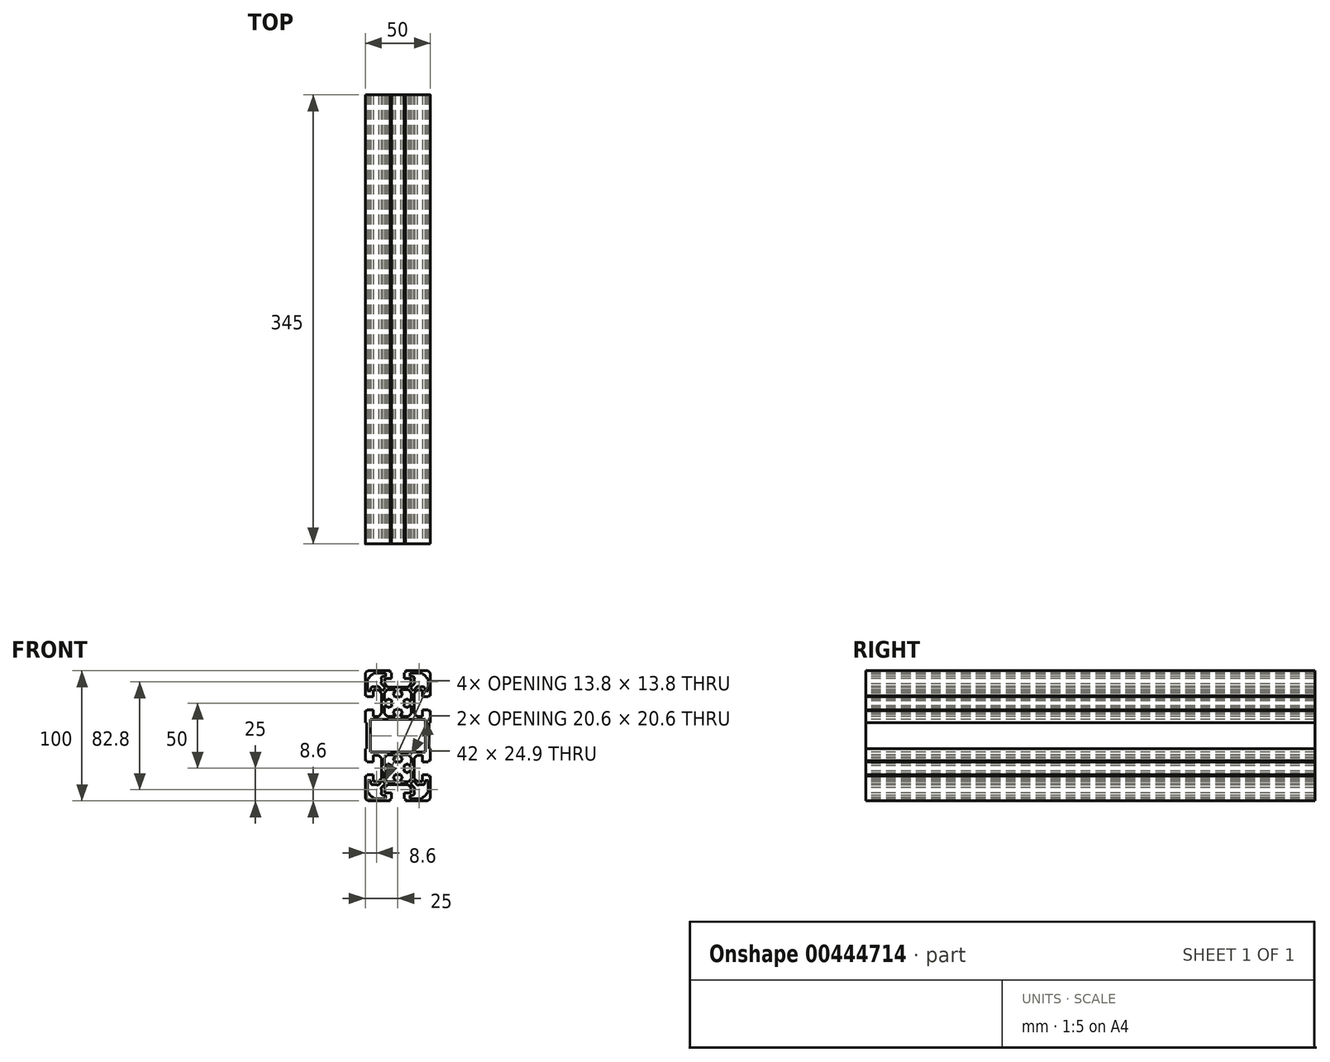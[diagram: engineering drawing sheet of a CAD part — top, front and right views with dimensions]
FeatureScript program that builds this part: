
annotation { "Feature Type Name" : "Feature", "Feature Type Description" : "" }
export const myFeature = defineFeature(function(context is Context, id is Id, definition is map)
    precondition{}
    {
        {
            var Q0;
            Q0=qCreatedBy(makeId("Front.planeOp"),FACE);
            var sketch = newSketch(context, id + "F0", { "sketchPlane" : qUnion([Q0])});
            skLineSegment(sketch, "E0", {"start": v(0, 0) * mm, "end": v(0, 25) * mm, "construction": true});
            skLineSegment(sketch, "E1", {"start": v(0, 0) * mm, "end": v(0, -25) * mm, "construction": true});
            skCircle(sketch, "E2", {"center": v(0, 25) * mm, "radius": 10 * mm});
            skCircle(sketch, "E3", {"center": v(0, -25) * mm, "radius": 10 * mm});
            skLineSegment(sketch, "E4.bottom", {"start": v(25, 50) * mm, "end": v(-25, 50) * mm});
            skLineSegment(sketch, "E4.top", {"start": v(25, -50) * mm, "end": v(-25, -50) * mm});
            skLineSegment(sketch, "E4.left", {"start": v(25, 50) * mm, "end": v(25, -50) * mm});
            skLineSegment(sketch, "E4.right", {"start": v(-25, 50) * mm, "end": v(-25, -50) * mm});
            skPoint(sketch, "E4.middle", {"position": v(0, 0) * mm});
            skSolve(sketch);
        }
        {
            var Q0;
            Q0=makeQuery(id+"F0.imprint","IMPRINT",FACE,{"disambiguationData":[TD([[makeQuery(id+"F0.imprint","IMPRINT",EDGE,{"derivedFrom":sQuery(id+"F0.wireOp",EDGE,"E2")}),-1.0]])]});
            cPlane(context, id + "F1", {"entities" : qUnion([Q0]), "cplaneType" : CPlaneType.OFFSET, "offset" : 25 * mm, "width" : 150 * mm, "height" : 150 * mm});
        }
        {
            var Q0;
            Q0=qCreatedBy(makeId("Front.planeOp"),FACE);
            var sketch = newSketch(context, id + "F2", { "sketchPlane" : qUnion([Q0])});
            skArc(sketch, "E5", {"start": v(-18.8, 37.67) * mm, "mid": v(-20.11, 37.42) * mm, "end": v(-20.7, 36.23) * mm});
            skArc(sketch, "E6", {"start": v(20.7, 36.23) * mm, "mid": v(20.11, 37.42) * mm, "end": v(18.8, 37.67) * mm});
            skArc(sketch, "E7", {"start": v(12.9, -40.52) * mm, "mid": v(12.51, -42.15) * mm, "end": v(12.67, -43.8) * mm});
            skArc(sketch, "E8", {"start": v(22, -50) * mm, "mid": v(24.12, -49.12) * mm, "end": v(25, -47) * mm});
            skArc(sketch, "E9", {"start": v(19, -47.27) * mm, "mid": v(21.04, -46.04) * mm, "end": v(22.27, -44) * mm});
            skArc(sketch, "E10", {"start": v(11.23, -45.7) * mm, "mid": v(12.42, -45.11) * mm, "end": v(12.67, -43.8) * mm});
            skArc(sketch, "E11", {"start": v(18.8, -37.67) * mm, "mid": v(20.11, -37.42) * mm, "end": v(20.7, -36.23) * mm});
            skArc(sketch, "E12", {"start": v(18.8, -37.67) * mm, "mid": v(17.14, -37.51) * mm, "end": v(15.52, -37.9) * mm});
            skArc(sketch, "E13", {"start": v(15.2, -37.85) * mm, "mid": v(15.35, -37.93) * mm, "end": v(15.52, -37.9) * mm});
            skArc(sketch, "E14", {"start": v(12.9, -40.52) * mm, "mid": v(12.93, -40.35) * mm, "end": v(12.84, -40.2) * mm});
            skArc(sketch, "E15", {"start": v(-4.53, -22.89) * mm, "mid": v(-5, -25) * mm, "end": v(-4.53, -27.11) * mm});
            skArc(sketch, "E16", {"start": v(4.53, -27.11) * mm, "mid": v(5, -25) * mm, "end": v(4.53, -22.89) * mm});
            skArc(sketch, "E17", {"start": v(-2.11, -29.53) * mm, "mid": v(0, -30) * mm, "end": v(2.11, -29.53) * mm});
            skArc(sketch, "E18", {"start": v(2.11, -20.47) * mm, "mid": v(0, -20) * mm, "end": v(-2.11, -20.47) * mm});
            skArc(sketch, "E19", {"start": v(-4.53, 27.11) * mm, "mid": v(-5, 25) * mm, "end": v(-4.53, 22.89) * mm});
            skArc(sketch, "E20", {"start": v(4.53, 22.89) * mm, "mid": v(5, 25) * mm, "end": v(4.53, 27.11) * mm});
            skArc(sketch, "E21", {"start": v(-2.11, 20.47) * mm, "mid": v(0, 20) * mm, "end": v(2.11, 20.47) * mm});
            skArc(sketch, "E22", {"start": v(15.52, 37.9) * mm, "mid": v(15.35, 37.93) * mm, "end": v(15.2, 37.84) * mm});
            skArc(sketch, "E23", {"start": v(15.52, 37.9) * mm, "mid": v(17.14, 37.51) * mm, "end": v(18.8, 37.67) * mm});
            skArc(sketch, "E24", {"start": v(2.11, 29.53) * mm, "mid": v(0, 30) * mm, "end": v(-2.11, 29.53) * mm});
            skArc(sketch, "E25", {"start": v(-12.67, -43.8) * mm, "mid": v(-12.51, -42.15) * mm, "end": v(-12.9, -40.52) * mm});
            skArc(sketch, "E26", {"start": v(-25, -47) * mm, "mid": v(-24.12, -49.12) * mm, "end": v(-22, -50) * mm});
            skArc(sketch, "E27", {"start": v(-12.67, -43.8) * mm, "mid": v(-12.42, -45.11) * mm, "end": v(-11.23, -45.7) * mm});
            skArc(sketch, "E28", {"start": v(-22.27, -44) * mm, "mid": v(-21.04, -46.04) * mm, "end": v(-19, -47.27) * mm});
            skArc(sketch, "E29", {"start": v(-20.7, -36.23) * mm, "mid": v(-20.11, -37.42) * mm, "end": v(-18.8, -37.67) * mm});
            skArc(sketch, "E30", {"start": v(-15.52, -37.9) * mm, "mid": v(-17.14, -37.51) * mm, "end": v(-18.8, -37.67) * mm});
            skArc(sketch, "E31", {"start": v(-12.84, -40.2) * mm, "mid": v(-12.93, -40.35) * mm, "end": v(-12.9, -40.52) * mm});
            skArc(sketch, "E32", {"start": v(-15.52, -37.9) * mm, "mid": v(-15.35, -37.93) * mm, "end": v(-15.2, -37.85) * mm});
            skArc(sketch, "E33", {"start": v(-18.8, 37.67) * mm, "mid": v(-17.14, 37.51) * mm, "end": v(-15.52, 37.9) * mm});
            skArc(sketch, "E34", {"start": v(-15.2, 37.84) * mm, "mid": v(-15.35, 37.93) * mm, "end": v(-15.52, 37.9) * mm});
            skArc(sketch, "E35", {"start": v(25, 47) * mm, "mid": v(24.12, 49.12) * mm, "end": v(22, 50) * mm});
            skArc(sketch, "E36", {"start": v(22.27, 44) * mm, "mid": v(21.04, 46.04) * mm, "end": v(19, 47.27) * mm});
            skArc(sketch, "E37", {"start": v(12.67, 43.8) * mm, "mid": v(12.42, 45.11) * mm, "end": v(11.23, 45.7) * mm});
            skArc(sketch, "E38", {"start": v(12.67, 43.8) * mm, "mid": v(12.51, 42.14) * mm, "end": v(12.9, 40.52) * mm});
            skArc(sketch, "E39", {"start": v(12.84, 40.2) * mm, "mid": v(12.93, 40.35) * mm, "end": v(12.9, 40.52) * mm});
            skArc(sketch, "E40", {"start": v(-22, 50) * mm, "mid": v(-24.12, 49.12) * mm, "end": v(-25, 47) * mm});
            skArc(sketch, "E41", {"start": v(-11.23, 45.7) * mm, "mid": v(-12.42, 45.11) * mm, "end": v(-12.67, 43.8) * mm});
            skArc(sketch, "E42", {"start": v(-12.9, 40.52) * mm, "mid": v(-12.93, 40.35) * mm, "end": v(-12.84, 40.2) * mm});
            skArc(sketch, "E43", {"start": v(-12.9, 40.52) * mm, "mid": v(-12.51, 42.14) * mm, "end": v(-12.67, 43.8) * mm});
            skArc(sketch, "E44", {"start": v(-19, 47.27) * mm, "mid": v(-21.04, 46.04) * mm, "end": v(-22.27, 44) * mm});
            skLineSegment(sketch, "E45", {"start": v(-9.54, 36.88) * mm, "end": v(-12.84, 40.2) * mm});
            skLineSegment(sketch, "E46", {"start": v(-25, 47) * mm, "end": v(-25, 30.8) * mm});
            skLineSegment(sketch, "E47", {"start": v(-23.3, 44) * mm, "end": v(-23.3, 34.5) * mm});
            skLineSegment(sketch, "E48", {"start": v(10.05, 39.8) * mm, "end": v(7.75, 37.5) * mm});
            skLineSegment(sketch, "E49", {"start": v(12.84, 40.2) * mm, "end": v(9.54, 36.88) * mm});
            skLineSegment(sketch, "E50", {"start": v(25, 30.8) * mm, "end": v(25, 47) * mm});
            skLineSegment(sketch, "E51", {"start": v(23.3, 34.5) * mm, "end": v(23.3, 44) * mm});
            skLineSegment(sketch, "E52", {"start": v(-7.75, 37.5) * mm, "end": v(-10.05, 39.8) * mm});
            skLineSegment(sketch, "E53", {"start": v(-2, 35.3) * mm, "end": v(-8.01, 35.3) * mm});
            skLineSegment(sketch, "E54", {"start": v(7.75, 37.5) * mm, "end": v(-7.75, 37.5) * mm});
            skLineSegment(sketch, "E55", {"start": v(-4.53, 22.89) * mm, "end": v(-7.7, 21.4) * mm});
            skLineSegment(sketch, "E56", {"start": v(-8.01, 14.7) * mm, "end": v(-2, 14.7) * mm});
            skLineSegment(sketch, "E57", {"start": v(-7.7, 28.6) * mm, "end": v(-4.53, 27.11) * mm});
            skLineSegment(sketch, "E58", {"start": v(-8.01, -35.3) * mm, "end": v(-2, -35.3) * mm});
            skLineSegment(sketch, "E59", {"start": v(-2, -14.7) * mm, "end": v(-8.01, -14.7) * mm});
            skLineSegment(sketch, "E60", {"start": v(-7.7, -21.4) * mm, "end": v(-4.53, -22.89) * mm});
            skLineSegment(sketch, "E61", {"start": v(-4.53, -27.11) * mm, "end": v(-7.7, -28.6) * mm});
            skLineSegment(sketch, "E62", {"start": v(-7.75, -37.5) * mm, "end": v(7.75, -37.5) * mm});
            skLineSegment(sketch, "E63", {"start": v(-5, -44) * mm, "end": v(-10.05, -44) * mm});
            skLineSegment(sketch, "E64", {"start": v(-22, -50) * mm, "end": v(-5.8, -50) * mm});
            skLineSegment(sketch, "E65", {"start": v(21, 12.45) * mm, "end": v(-21, 12.45) * mm});
            skLineSegment(sketch, "E66", {"start": v(-21, -12.45) * mm, "end": v(21, -12.45) * mm});
            skLineSegment(sketch, "E67", {"start": v(24, -10) * mm, "end": v(24, 10) * mm});
            skLineSegment(sketch, "E68", {"start": v(21, -12.45) * mm, "end": v(21, 12.45) * mm});
            skLineSegment(sketch, "E69", {"start": v(-3.6, -32.7) * mm, "end": v(-2.11, -29.53) * mm});
            skLineSegment(sketch, "E70", {"start": v(2.11, -29.53) * mm, "end": v(3.6, -32.7) * mm});
            skLineSegment(sketch, "E71", {"start": v(10.3, -33.01) * mm, "end": v(10.3, -27) * mm});
            skLineSegment(sketch, "E72", {"start": v(12.5, -32.75) * mm, "end": v(12.5, -17.25) * mm});
            skLineSegment(sketch, "E73", {"start": v(19, -30) * mm, "end": v(19, -35.05) * mm});
            skLineSegment(sketch, "E74", {"start": v(25, -47) * mm, "end": v(25, -30.8) * mm});
            skLineSegment(sketch, "E75", {"start": v(10.05, -39.8) * mm, "end": v(10.05, -44) * mm});
            skLineSegment(sketch, "E76", {"start": v(23.3, -44) * mm, "end": v(23.3, -34.5) * mm});
            skLineSegment(sketch, "E77", {"start": v(5.8, -50) * mm, "end": v(22, -50) * mm});
            skLineSegment(sketch, "E78", {"start": v(9.5, -48.3) * mm, "end": v(19, -48.3) * mm});
            skLineSegment(sketch, "E79", {"start": v(22.27, -44) * mm, "end": v(23.3, -44) * mm});
            skLineSegment(sketch, "E80", {"start": v(19, -48.3) * mm, "end": v(19, -47.27) * mm});
            skLineSegment(sketch, "E81", {"start": v(-5.8, -50) * mm, "end": v(-5.8, -48.5) * mm});
            skLineSegment(sketch, "E82", {"start": v(5.8, -48.5) * mm, "end": v(5.8, -50) * mm});
            skLineSegment(sketch, "E83", {"start": v(10.05, -44) * mm, "end": v(5, -44) * mm});
            skLineSegment(sketch, "E84", {"start": v(11.23, -45.7) * mm, "end": v(9.5, -45.7) * mm});
            skLineSegment(sketch, "E85", {"start": v(5, -48.5) * mm, "end": v(5.8, -48.5) * mm});
            skLineSegment(sketch, "E86", {"start": v(5, -44) * mm, "end": v(5, -48.5) * mm});
            skLineSegment(sketch, "E87", {"start": v(9.5, -45.7) * mm, "end": v(9.5, -48.3) * mm});
            skLineSegment(sketch, "E88", {"start": v(-5.8, -48.5) * mm, "end": v(-5, -48.5) * mm});
            skLineSegment(sketch, "E89", {"start": v(-5, -48.5) * mm, "end": v(-5, -44) * mm});
            skLineSegment(sketch, "E90", {"start": v(14.8, -35.05) * mm, "end": v(12.5, -32.75) * mm});
            skLineSegment(sketch, "E91", {"start": v(15.2, -37.85) * mm, "end": v(11.88, -34.54) * mm});
            skLineSegment(sketch, "E92", {"start": v(19, -35.05) * mm, "end": v(14.8, -35.05) * mm});
            skLineSegment(sketch, "E93", {"start": v(20.7, -34.5) * mm, "end": v(20.7, -36.23) * mm});
            skLineSegment(sketch, "E94", {"start": v(23.3, -34.5) * mm, "end": v(20.7, -34.5) * mm});
            skLineSegment(sketch, "E95", {"start": v(9.54, -36.89) * mm, "end": v(12.84, -40.2) * mm});
            skLineSegment(sketch, "E96", {"start": v(7.75, -37.5) * mm, "end": v(10.05, -39.8) * mm});
            skLineSegment(sketch, "E97", {"start": v(3.6, -32.7) * mm, "end": v(2, -33.45) * mm});
            skLineSegment(sketch, "E98", {"start": v(2, -35.3) * mm, "end": v(8.01, -35.3) * mm});
            skLineSegment(sketch, "E99", {"start": v(11.88, -34.54) * mm, "end": v(9.54, -36.89) * mm});
            skLineSegment(sketch, "E100", {"start": v(8.01, -35.3) * mm, "end": v(10.3, -33.01) * mm});
            skLineSegment(sketch, "E101", {"start": v(-2, -35.3) * mm, "end": v(-2, -33.45) * mm});
            skLineSegment(sketch, "E102", {"start": v(-2, -33.45) * mm, "end": v(-3.6, -32.7) * mm});
            skLineSegment(sketch, "E103", {"start": v(2, -33.45) * mm, "end": v(2, -35.3) * mm});
            skLineSegment(sketch, "E104", {"start": v(-2.11, -20.47) * mm, "end": v(-3.6, -17.3) * mm});
            skLineSegment(sketch, "E105", {"start": v(10.3, -23) * mm, "end": v(10.3, -16.99) * mm});
            skLineSegment(sketch, "E106", {"start": v(3.6, -17.3) * mm, "end": v(2.11, -20.47) * mm});
            skLineSegment(sketch, "E107", {"start": v(19, -14.95) * mm, "end": v(19, -20) * mm});
            skLineSegment(sketch, "E108", {"start": v(23.5, -20) * mm, "end": v(23.5, -19.2) * mm});
            skLineSegment(sketch, "E109", {"start": v(25, -30.8) * mm, "end": v(23.5, -30.8) * mm});
            skLineSegment(sketch, "E110", {"start": v(23.5, -30.8) * mm, "end": v(23.5, -30) * mm});
            skLineSegment(sketch, "E111", {"start": v(23.5, -30) * mm, "end": v(19, -30) * mm});
            skLineSegment(sketch, "E112", {"start": v(19, -20) * mm, "end": v(23.5, -20) * mm});
            skLineSegment(sketch, "E113", {"start": v(10.3, -27) * mm, "end": v(8.45, -27) * mm});
            skLineSegment(sketch, "E114", {"start": v(8.45, -27) * mm, "end": v(7.7, -28.6) * mm});
            skLineSegment(sketch, "E115", {"start": v(7.7, -28.6) * mm, "end": v(4.53, -27.11) * mm});
            skLineSegment(sketch, "E116", {"start": v(4.53, -22.89) * mm, "end": v(7.7, -21.4) * mm});
            skLineSegment(sketch, "E117", {"start": v(7.7, -21.4) * mm, "end": v(8.45, -23) * mm});
            skLineSegment(sketch, "E118", {"start": v(8.45, -23) * mm, "end": v(10.3, -23) * mm});
            skLineSegment(sketch, "E119", {"start": v(12.5, -17.25) * mm, "end": v(14.8, -14.95) * mm});
            skLineSegment(sketch, "E120", {"start": v(25, -19.2) * mm, "end": v(25, -10) * mm});
            skLineSegment(sketch, "E121", {"start": v(23.5, -19.2) * mm, "end": v(25, -19.2) * mm});
            skLineSegment(sketch, "E122", {"start": v(14.8, -14.95) * mm, "end": v(19, -14.95) * mm});
            skLineSegment(sketch, "E123", {"start": v(25, -10) * mm, "end": v(24, -10) * mm});
            skLineSegment(sketch, "E124", {"start": v(8.01, -14.7) * mm, "end": v(2, -14.7) * mm});
            skLineSegment(sketch, "E125", {"start": v(2, -16.55) * mm, "end": v(3.6, -17.3) * mm});
            skLineSegment(sketch, "E126", {"start": v(10.3, -16.99) * mm, "end": v(8.01, -14.7) * mm});
            skLineSegment(sketch, "E127", {"start": v(-3.6, -17.3) * mm, "end": v(-2, -16.55) * mm});
            skLineSegment(sketch, "E128", {"start": v(-2, -16.55) * mm, "end": v(-2, -14.7) * mm});
            skLineSegment(sketch, "E129", {"start": v(2, -14.7) * mm, "end": v(2, -16.55) * mm});
            skLineSegment(sketch, "E130", {"start": v(-2, 14.7) * mm, "end": v(-2, 16.55) * mm});
            skLineSegment(sketch, "E131", {"start": v(2, 16.55) * mm, "end": v(2, 14.7) * mm});
            skLineSegment(sketch, "E132", {"start": v(8.01, 14.7) * mm, "end": v(10.3, 16.99) * mm});
            skLineSegment(sketch, "E133", {"start": v(25, 10) * mm, "end": v(25, 19.2) * mm});
            skLineSegment(sketch, "E134", {"start": v(24, 10) * mm, "end": v(25, 10) * mm});
            skLineSegment(sketch, "E135", {"start": v(2, 14.7) * mm, "end": v(8.01, 14.7) * mm});
            skLineSegment(sketch, "E136", {"start": v(12.5, 17.25) * mm, "end": v(12.5, 32.75) * mm});
            skLineSegment(sketch, "E137", {"start": v(14.8, 14.95) * mm, "end": v(12.5, 17.25) * mm});
            skLineSegment(sketch, "E138", {"start": v(25, 19.2) * mm, "end": v(23.5, 19.2) * mm});
            skLineSegment(sketch, "E139", {"start": v(19, 14.95) * mm, "end": v(14.8, 14.95) * mm});
            skLineSegment(sketch, "E140", {"start": v(19, 20) * mm, "end": v(19, 14.95) * mm});
            skLineSegment(sketch, "E141", {"start": v(23.5, 19.2) * mm, "end": v(23.5, 20) * mm});
            skLineSegment(sketch, "E142", {"start": v(23.5, 20) * mm, "end": v(19, 20) * mm});
            skLineSegment(sketch, "E143", {"start": v(10.3, 16.99) * mm, "end": v(10.3, 23) * mm});
            skLineSegment(sketch, "E144", {"start": v(2.11, 20.47) * mm, "end": v(3.6, 17.3) * mm});
            skLineSegment(sketch, "E145", {"start": v(3.6, 17.3) * mm, "end": v(2, 16.55) * mm});
            skLineSegment(sketch, "E146", {"start": v(-2, 16.55) * mm, "end": v(-3.6, 17.3) * mm});
            skLineSegment(sketch, "E147", {"start": v(-3.6, 17.3) * mm, "end": v(-2.11, 20.47) * mm});
            skLineSegment(sketch, "E148", {"start": v(10.3, 23) * mm, "end": v(8.45, 23) * mm});
            skLineSegment(sketch, "E149", {"start": v(8.45, 23) * mm, "end": v(7.7, 21.4) * mm});
            skLineSegment(sketch, "E150", {"start": v(7.7, 21.4) * mm, "end": v(4.53, 22.89) * mm});
            skLineSegment(sketch, "E151", {"start": v(12.5, 32.75) * mm, "end": v(14.8, 35.05) * mm});
            skLineSegment(sketch, "E152", {"start": v(11.88, 34.54) * mm, "end": v(15.2, 37.84) * mm});
            skLineSegment(sketch, "E153", {"start": v(19, 35.05) * mm, "end": v(19, 30) * mm});
            skLineSegment(sketch, "E154", {"start": v(23.5, 30.8) * mm, "end": v(25, 30.8) * mm});
            skLineSegment(sketch, "E155", {"start": v(23.5, 30) * mm, "end": v(23.5, 30.8) * mm});
            skLineSegment(sketch, "E156", {"start": v(19, 30) * mm, "end": v(23.5, 30) * mm});
            skLineSegment(sketch, "E157", {"start": v(14.8, 35.05) * mm, "end": v(19, 35.05) * mm});
            skLineSegment(sketch, "E158", {"start": v(20.7, 34.5) * mm, "end": v(23.3, 34.5) * mm});
            skLineSegment(sketch, "E159", {"start": v(20.7, 36.23) * mm, "end": v(20.7, 34.5) * mm});
            skLineSegment(sketch, "E160", {"start": v(-2.11, 29.53) * mm, "end": v(-3.6, 32.7) * mm});
            skLineSegment(sketch, "E161", {"start": v(10.3, 27) * mm, "end": v(10.3, 33.01) * mm});
            skLineSegment(sketch, "E162", {"start": v(3.6, 32.7) * mm, "end": v(2.11, 29.53) * mm});
            skLineSegment(sketch, "E163", {"start": v(4.53, 27.11) * mm, "end": v(7.7, 28.6) * mm});
            skLineSegment(sketch, "E164", {"start": v(7.7, 28.6) * mm, "end": v(8.45, 27) * mm});
            skLineSegment(sketch, "E165", {"start": v(8.45, 27) * mm, "end": v(10.3, 27) * mm});
            skLineSegment(sketch, "E166", {"start": v(8.01, 35.3) * mm, "end": v(2, 35.3) * mm});
            skLineSegment(sketch, "E167", {"start": v(2, 33.45) * mm, "end": v(3.6, 32.7) * mm});
            skLineSegment(sketch, "E168", {"start": v(10.3, 33.01) * mm, "end": v(8.01, 35.3) * mm});
            skLineSegment(sketch, "E169", {"start": v(9.54, 36.88) * mm, "end": v(11.88, 34.54) * mm});
            skLineSegment(sketch, "E170", {"start": v(-3.6, 32.7) * mm, "end": v(-2, 33.45) * mm});
            skLineSegment(sketch, "E171", {"start": v(2, 35.3) * mm, "end": v(2, 33.45) * mm});
            skLineSegment(sketch, "E172", {"start": v(-2, 33.45) * mm, "end": v(-2, 35.3) * mm});
            skLineSegment(sketch, "E173", {"start": v(-24, 10) * mm, "end": v(-24, -10) * mm});
            skLineSegment(sketch, "E174", {"start": v(-21, 12.45) * mm, "end": v(-21, -12.45) * mm});
            skLineSegment(sketch, "E175", {"start": v(-19, -35.05) * mm, "end": v(-19, -30) * mm});
            skLineSegment(sketch, "E176", {"start": v(-12.5, -17.25) * mm, "end": v(-12.5, -32.75) * mm});
            skLineSegment(sketch, "E177", {"start": v(-10.3, -27) * mm, "end": v(-10.3, -33.01) * mm});
            skLineSegment(sketch, "E178", {"start": v(-25, -30.8) * mm, "end": v(-25, -47) * mm});
            skLineSegment(sketch, "E179", {"start": v(-23.3, -34.5) * mm, "end": v(-23.3, -44) * mm});
            skLineSegment(sketch, "E180", {"start": v(-10.05, -44) * mm, "end": v(-10.05, -39.8) * mm});
            skLineSegment(sketch, "E181", {"start": v(-19, -48.3) * mm, "end": v(-9.5, -48.3) * mm});
            skLineSegment(sketch, "E182", {"start": v(-9.5, -45.7) * mm, "end": v(-11.23, -45.7) * mm});
            skLineSegment(sketch, "E183", {"start": v(-9.5, -48.3) * mm, "end": v(-9.5, -45.7) * mm});
            skLineSegment(sketch, "E184", {"start": v(-23.3, -44) * mm, "end": v(-22.27, -44) * mm});
            skLineSegment(sketch, "E185", {"start": v(-19, -47.27) * mm, "end": v(-19, -48.3) * mm});
            skLineSegment(sketch, "E186", {"start": v(-12.84, -40.2) * mm, "end": v(-9.54, -36.89) * mm});
            skLineSegment(sketch, "E187", {"start": v(-11.88, -34.54) * mm, "end": v(-15.2, -37.85) * mm});
            skLineSegment(sketch, "E188", {"start": v(-10.05, -39.8) * mm, "end": v(-7.75, -37.5) * mm});
            skLineSegment(sketch, "E189", {"start": v(-14.8, -35.05) * mm, "end": v(-19, -35.05) * mm});
            skLineSegment(sketch, "E190", {"start": v(-12.5, -32.75) * mm, "end": v(-14.8, -35.05) * mm});
            skLineSegment(sketch, "E191", {"start": v(-9.54, -36.89) * mm, "end": v(-11.88, -34.54) * mm});
            skLineSegment(sketch, "E192", {"start": v(-10.3, -33.01) * mm, "end": v(-8.01, -35.3) * mm});
            skLineSegment(sketch, "E193", {"start": v(-20.7, -36.23) * mm, "end": v(-20.7, -34.5) * mm});
            skLineSegment(sketch, "E194", {"start": v(-20.7, -34.5) * mm, "end": v(-23.3, -34.5) * mm});
            skLineSegment(sketch, "E195", {"start": v(-23.5, -19.2) * mm, "end": v(-23.5, -20) * mm});
            skLineSegment(sketch, "E196", {"start": v(-19, -20) * mm, "end": v(-19, -14.95) * mm});
            skLineSegment(sketch, "E197", {"start": v(-10.3, -16.99) * mm, "end": v(-10.3, -23) * mm});
            skLineSegment(sketch, "E198", {"start": v(-7.7, -28.6) * mm, "end": v(-8.45, -27) * mm});
            skLineSegment(sketch, "E199", {"start": v(-8.45, -27) * mm, "end": v(-10.3, -27) * mm});
            skLineSegment(sketch, "E200", {"start": v(-23.5, -30.8) * mm, "end": v(-25, -30.8) * mm});
            skLineSegment(sketch, "E201", {"start": v(-23.5, -30) * mm, "end": v(-23.5, -30.8) * mm});
            skLineSegment(sketch, "E202", {"start": v(-19, -30) * mm, "end": v(-23.5, -30) * mm});
            skLineSegment(sketch, "E203", {"start": v(-8.45, -23) * mm, "end": v(-7.7, -21.4) * mm});
            skLineSegment(sketch, "E204", {"start": v(-10.3, -23) * mm, "end": v(-8.45, -23) * mm});
            skLineSegment(sketch, "E205", {"start": v(-23.5, -20) * mm, "end": v(-19, -20) * mm});
            skLineSegment(sketch, "E206", {"start": v(-25, -10) * mm, "end": v(-25, -19.2) * mm});
            skLineSegment(sketch, "E207", {"start": v(-19, -14.95) * mm, "end": v(-14.8, -14.95) * mm});
            skLineSegment(sketch, "E208", {"start": v(-14.8, -14.95) * mm, "end": v(-12.5, -17.25) * mm});
            skLineSegment(sketch, "E209", {"start": v(-8.01, -14.7) * mm, "end": v(-10.3, -16.99) * mm});
            skLineSegment(sketch, "E210", {"start": v(-25, -19.2) * mm, "end": v(-23.5, -19.2) * mm});
            skLineSegment(sketch, "E211", {"start": v(-24, -10) * mm, "end": v(-25, -10) * mm});
            skLineSegment(sketch, "E212", {"start": v(-25, 19.2) * mm, "end": v(-25, 10) * mm});
            skLineSegment(sketch, "E213", {"start": v(-10.3, 16.99) * mm, "end": v(-8.01, 14.7) * mm});
            skLineSegment(sketch, "E214", {"start": v(-25, 10) * mm, "end": v(-24, 10) * mm});
            skLineSegment(sketch, "E215", {"start": v(-12.5, 32.75) * mm, "end": v(-12.5, 17.25) * mm});
            skLineSegment(sketch, "E216", {"start": v(-10.3, 23) * mm, "end": v(-10.3, 16.99) * mm});
            skLineSegment(sketch, "E217", {"start": v(-14.8, 14.95) * mm, "end": v(-19, 14.95) * mm});
            skLineSegment(sketch, "E218", {"start": v(-12.5, 17.25) * mm, "end": v(-14.8, 14.95) * mm});
            skLineSegment(sketch, "E219", {"start": v(-23.5, 19.2) * mm, "end": v(-25, 19.2) * mm});
            skLineSegment(sketch, "E220", {"start": v(-23.5, 20) * mm, "end": v(-23.5, 19.2) * mm});
            skLineSegment(sketch, "E221", {"start": v(-19, 14.95) * mm, "end": v(-19, 20) * mm});
            skLineSegment(sketch, "E222", {"start": v(-19, 20) * mm, "end": v(-23.5, 20) * mm});
            skLineSegment(sketch, "E223", {"start": v(-7.7, 21.4) * mm, "end": v(-8.45, 23) * mm});
            skLineSegment(sketch, "E224", {"start": v(-8.45, 23) * mm, "end": v(-10.3, 23) * mm});
            skLineSegment(sketch, "E225", {"start": v(-10.3, 33.01) * mm, "end": v(-10.3, 27) * mm});
            skLineSegment(sketch, "E226", {"start": v(-19, 30) * mm, "end": v(-19, 35.05) * mm});
            skLineSegment(sketch, "E227", {"start": v(-8.45, 27) * mm, "end": v(-7.7, 28.6) * mm});
            skLineSegment(sketch, "E228", {"start": v(-10.3, 27) * mm, "end": v(-8.45, 27) * mm});
            skLineSegment(sketch, "E229", {"start": v(-23.5, 30.8) * mm, "end": v(-23.5, 30) * mm});
            skLineSegment(sketch, "E230", {"start": v(-25, 30.8) * mm, "end": v(-23.5, 30.8) * mm});
            skLineSegment(sketch, "E231", {"start": v(-23.5, 30) * mm, "end": v(-19, 30) * mm});
            skLineSegment(sketch, "E232", {"start": v(-19, 35.05) * mm, "end": v(-14.8, 35.05) * mm});
            skLineSegment(sketch, "E233", {"start": v(-14.8, 35.05) * mm, "end": v(-12.5, 32.75) * mm});
            skLineSegment(sketch, "E234", {"start": v(-15.2, 37.84) * mm, "end": v(-11.88, 34.54) * mm});
            skLineSegment(sketch, "E235", {"start": v(-11.88, 34.54) * mm, "end": v(-9.54, 36.88) * mm});
            skLineSegment(sketch, "E236", {"start": v(-8.01, 35.3) * mm, "end": v(-10.3, 33.01) * mm});
            skLineSegment(sketch, "E237", {"start": v(-23.3, 34.5) * mm, "end": v(-20.7, 34.5) * mm});
            skLineSegment(sketch, "E238", {"start": v(-20.7, 34.5) * mm, "end": v(-20.7, 36.23) * mm});
            skLineSegment(sketch, "E239", {"start": v(-5.8, 50) * mm, "end": v(-22, 50) * mm});
            skLineSegment(sketch, "E240", {"start": v(-10.05, 44) * mm, "end": v(-5, 44) * mm});
            skLineSegment(sketch, "E241", {"start": v(-5.8, 48.5) * mm, "end": v(-5.8, 50) * mm});
            skLineSegment(sketch, "E242", {"start": v(5.8, 50) * mm, "end": v(5.8, 48.5) * mm});
            skLineSegment(sketch, "E243", {"start": v(19, 48.3) * mm, "end": v(9.5, 48.3) * mm});
            skLineSegment(sketch, "E244", {"start": v(19, 47.27) * mm, "end": v(19, 48.3) * mm});
            skLineSegment(sketch, "E245", {"start": v(23.3, 44) * mm, "end": v(22.27, 44) * mm});
            skLineSegment(sketch, "E246", {"start": v(10.05, 44) * mm, "end": v(10.05, 39.8) * mm});
            skLineSegment(sketch, "E247", {"start": v(5, 44) * mm, "end": v(10.05, 44) * mm});
            skLineSegment(sketch, "E248", {"start": v(5, 48.5) * mm, "end": v(5, 44) * mm});
            skLineSegment(sketch, "E249", {"start": v(5.8, 48.5) * mm, "end": v(5, 48.5) * mm});
            skLineSegment(sketch, "E250", {"start": v(9.5, 48.3) * mm, "end": v(9.5, 45.7) * mm});
            skLineSegment(sketch, "E251", {"start": v(9.5, 45.7) * mm, "end": v(11.23, 45.7) * mm});
            skLineSegment(sketch, "E252", {"start": v(-5, 48.5) * mm, "end": v(-5.8, 48.5) * mm});
            skLineSegment(sketch, "E253", {"start": v(-5, 44) * mm, "end": v(-5, 48.5) * mm});
            skLineSegment(sketch, "E254", {"start": v(22, 50) * mm, "end": v(5.8, 50) * mm});
            skLineSegment(sketch, "E255", {"start": v(-10.05, 39.8) * mm, "end": v(-10.05, 44) * mm});
            skLineSegment(sketch, "E256", {"start": v(-9.5, 48.3) * mm, "end": v(-19, 48.3) * mm});
            skLineSegment(sketch, "E257", {"start": v(-11.23, 45.7) * mm, "end": v(-9.5, 45.7) * mm});
            skLineSegment(sketch, "E258", {"start": v(-9.5, 45.7) * mm, "end": v(-9.5, 48.3) * mm});
            skLineSegment(sketch, "E259", {"start": v(-22.27, 44) * mm, "end": v(-23.3, 44) * mm});
            skLineSegment(sketch, "E260", {"start": v(-19, 48.3) * mm, "end": v(-19, 47.27) * mm});
            skLineSegment(sketch, "E261", {"start": v(31.28, 0) * mm, "end": v(-51.84, 0) * mm});
            skLineSegment(sketch, "E262", {"start": v(0, 67.76) * mm, "end": v(0, -64.44) * mm});
            skSolve(sketch);
        }
        {
            var Q0;
            Q0=makeQuery(id+"F2.imprint","IMPRINT",FACE,{"disambiguationData":[TD([[makeQuery(id+"F2.imprint","IMPRINT",EDGE,{"derivedFrom":sQuery(id+"F2.wireOp",EDGE,"E6")}),1.0]])]});
            var Q1;
            Q1=makeQuery(id+"F2.imprint","IMPRINT",FACE,{"disambiguationData":[TD([[makeQuery(id+"F2.imprint","IMPRINT",EDGE,{"derivedFrom":sQuery(id+"F2.wireOp",EDGE,"E5")}),1.0]])]});
            var Q2;
            Q2=makeQuery(id+"F2.imprint","IMPRINT",FACE,{"disambiguationData":[TD([[makeQuery(id+"F2.imprint","IMPRINT",EDGE,{"derivedFrom":sQuery(id+"F2.wireOp",EDGE,"E7")}),-1.0]])]});
            var Q3;
            Q3=makeQuery(id+"F2.imprint","IMPRINT",FACE,{"disambiguationData":[TD([[makeQuery(id+"F2.imprint","IMPRINT",EDGE,{"derivedFrom":sQuery(id+"F2.wireOp",EDGE,"E15")}),-1.0]])]});
            extrude(context, id + "F3", {"entities" : qUnion([Q0, Q1, Q2, Q3]), "oppositeDirection" : true, "depth" : 345 * mm});
        }
    });
